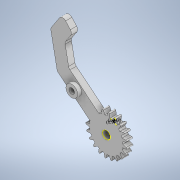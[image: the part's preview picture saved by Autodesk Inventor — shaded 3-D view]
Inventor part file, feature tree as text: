
AUTODESK INVENTOR PART (.ipt)
format: ipt  version: 2021 (Build 250183000, 183)  size: 269,824 bytes
history: native  units: mm
features: sketch x3, extrude x2
ambient origin geometry x8: Origin, YZ Plane, XZ Plane, XY Plane, X Axis, Y Axis, Z Axis, Center Point
bodies: Solid1 (feature_tree)
feature tree (5):
  extrude  "Extrusion1"  Depth=20.0mm
  extrude  "Extrusion2"  Depth=4.415mm
  sketch  "Sketch3"  dims[d4=28.900907mm d6=10.294216mm d8=2.5mm d11=11.34mm d13=17.650515mm d14=2.5mm d16=5.75mm d17=9.873328mm d18=2.5mm d22=9.37mm d23=8.3mm d25=8.83mm d26=2.5mm d27=3.5mm d34=11.05317mm d41=0.5mm d44=170.0mm d46=48.869219mm d48=4.0mm d49=0.0mm d50=7.5mm d51=2.5mm d52=0.0mm d53=1.990639mm d54=2.046556mm]
  sketch  "Sketch1"  dims[d0=5.0mm d1=20.0mm]
  sketch  "Sketch2"  dims[d2=24.631832mm d3=4.415mm]
